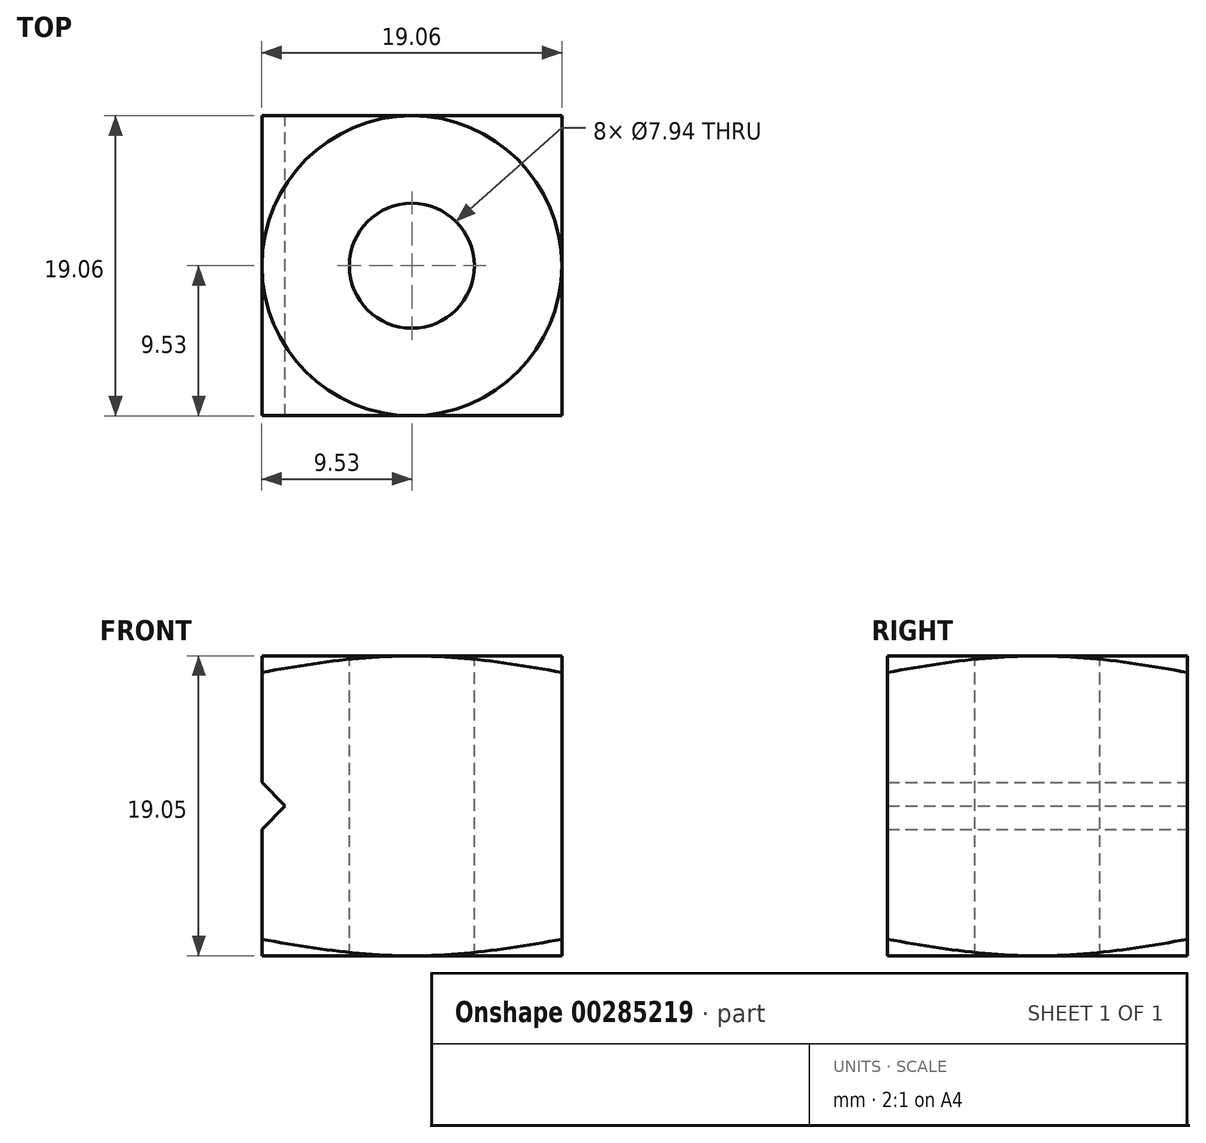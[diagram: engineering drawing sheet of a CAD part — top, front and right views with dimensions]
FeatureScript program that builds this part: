
annotation { "Feature Type Name" : "Feature", "Feature Type Description" : "" }
export const myFeature = defineFeature(function(context is Context, id is Id, definition is map)
    precondition{}
    {
        {
            var Q0;
            Q0=qCreatedBy(makeId("Top.planeOp"),FACE);
            var sketch = newSketch(context, id + "F0", { "sketchPlane" : qUnion([Q0])});
            skLineSegment(sketch, "E0.bottom", {"start": v(9.52, -9.52) * mm, "end": v(-9.53, -9.52) * mm});
            skLineSegment(sketch, "E0.top", {"start": v(9.52, 9.53) * mm, "end": v(-9.53, 9.53) * mm});
            skLineSegment(sketch, "E0.left", {"start": v(9.52, -9.52) * mm, "end": v(9.52, 9.53) * mm});
            skLineSegment(sketch, "E0.right", {"start": v(-9.53, -9.52) * mm, "end": v(-9.53, 9.52) * mm});
            skPoint(sketch, "E0.middle", {"position": v(0, 0) * mm});
            skSolve(sketch);
        }
        {
            var Q0;
            Q0=qSketchRegion(id+"F0",true);
            extrude(context, id + "F1", {"entities" : qUnion([Q0]), "depth" : 19.05 * mm});
        }
        {
            var Q0;
            Q0=makeQuery(id+"F1.opExtrude","CAP_FACE",FACE,{"disambiguationData":[OSD([sQuery(id+"F0.wireOp",EDGE,"E0.bottom"),sQuery(id+"F0.wireOp",EDGE,"E0.top"),sQuery(id+"F0.wireOp",EDGE,"E0.left"),sQuery(id+"F0.wireOp",EDGE,"E0.right")])],"isStart":false});
            var sketch = newSketch(context, id + "F2", { "sketchPlane" : qUnion([Q0])});
            skCircle(sketch, "E1", {"center": v(0, 0) * mm, "radius": 9.53 * mm});
            skCircle(sketch, "E2", {"center": v(0, 0) * mm, "radius": 3.97 * mm});
            skSolve(sketch);
        }
        {
            var Q0;
            Q0=makeQuery(id+"F2.imprint","IMPRINT",FACE,{"disambiguationData":[TD([[makeQuery(id+"F2.imprint","IMPRINT",EDGE,{"derivedFrom":sQuery(id+"F2.wireOp",EDGE,"E2")}),1.0]])]});
            var Q1;
            Q1=sQuery(id+"F2.wireOp",EDGE,"E2");
            extrude(context, id + "F3", {"entities" : qUnion([Q0]), "operationType" : NewBodyOperationType.REMOVE, "surfaceEntities" : qUnion([Q1]), "endBound" : BoundingType.THROUGH_ALL, "oppositeDirection" : true, "depth" : 25.4 * mm});
        }
        {
            var Q0;
            Q0=qCreatedBy(makeId("Right.planeOp"),FACE);
            var sketch = newSketch(context, id + "F4", { "sketchPlane" : qUnion([Q0])});
            skLineSegment(sketch, "E3.0", {"start": v(-9.53, 19.05) * mm, "end": v(9.53, 19.05) * mm});
            skLineSegment(sketch, "E4.0", {"start": v(9.53, 19.05) * mm, "end": v(9.53, 0) * mm});
            skLineSegment(sketch, "E5", {"start": v(9.53, 19.05) * mm, "end": v(24.77, 19.05) * mm});
            skLineSegment(sketch, "E6", {"start": v(24.77, 19.05) * mm, "end": v(24.77, 14.97) * mm});
            skLineSegment(sketch, "E7", {"start": v(9.53, 19.05) * mm, "end": v(24.77, 14.97) * mm});
            skSolve(sketch);
        }
        {
            var Q0;
            Q0=makeQuery(id+"F4.imprint","IMPRINT",FACE,{"disambiguationData":[TD([[makeQuery(id+"F4.imprint","IMPRINT",EDGE,{"derivedFrom":sQuery(id+"F4.wireOp",EDGE,"E5")}),-1.0]])]});
            var Q1;
            Q1=sQuery(id+"F2.wireOp",EDGE,"E1");
            revolve(context, id + "F5", {"operationType" : NewBodyOperationType.REMOVE, "entities" : qUnion([Q0]), "axis" : qUnion([Q1]), "revolveType" : RevolveType.FULL, "oppositeDirection" : true});
        }
        {
            var Q0;
            Q0=makeQuery(id+"F1.opExtrude","CAP_FACE",FACE,{"disambiguationData":[OSD([sQuery(id+"F0.wireOp",EDGE,"E0.bottom"),sQuery(id+"F0.wireOp",EDGE,"E0.top"),sQuery(id+"F0.wireOp",EDGE,"E0.left"),sQuery(id+"F0.wireOp",EDGE,"E0.right")])],"isStart":true});
            var sketch = newSketch(context, id + "F6", { "sketchPlane" : qUnion([Q0])});
            skCircle(sketch, "E8.0", {"center": v(0, 0) * mm, "radius": 9.53 * mm});
            skSolve(sketch);
        }
        {
            var Q0;
            Q0=qCreatedBy(makeId("Right.planeOp"),FACE);
            var sketch = newSketch(context, id + "F7", { "sketchPlane" : qUnion([Q0])});
            skLineSegment(sketch, "E9.0", {"start": v(-9.53, 0) * mm, "end": v(9.53, 0) * mm});
            skLineSegment(sketch, "E10", {"start": v(-9.53, 0) * mm, "end": v(-22.83, 0) * mm});
            skLineSegment(sketch, "E11", {"start": v(-22.83, 0) * mm, "end": v(-22.83, 3.57) * mm});
            skLineSegment(sketch, "E12", {"start": v(-22.83, 3.57) * mm, "end": v(-9.53, 0) * mm});
            skSolve(sketch);
        }
        {
            var Q0;
            Q0=makeQuery(id+"F7.imprint","IMPRINT",FACE,{"disambiguationData":[TD([[makeQuery(id+"F7.imprint","IMPRINT",EDGE,{"derivedFrom":sQuery(id+"F7.wireOp",EDGE,"E10")}),-1.0]])]});
            var Q1;
            Q1=sQuery(id+"F6.wireOp",EDGE,"E8.0");
            revolve(context, id + "F8", {"operationType" : NewBodyOperationType.REMOVE, "entities" : qUnion([Q0]), "axis" : qUnion([Q1]), "revolveType" : RevolveType.FULL, "oppositeDirection" : true});
        }
        {
            var Q0;
            Q0=qCreatedBy(makeId("Front.planeOp"),FACE);
            var sketch = newSketch(context, id + "F9", { "sketchPlane" : qUnion([Q0])});
            skLineSegment(sketch, "E13.0.0", {"start": v(-9.53, 18) * mm, "end": v(-9.53, 1.06) * mm});
            skFitSpline(sketch, "E13.0.1", {"points": [v(-9.53, 1.06) * mm, v(-7.95, 0.76) * mm, v(-5.57, 0.36) * mm, v(-2.39, 0.05) * mm, v(-0.8, 0) * mm, v(0, 0) * mm]});
            skFitSpline(sketch, "E13.0.2", {"points": [v(0, 0) * mm, v(0.8, 0) * mm, v(2.39, 0.05) * mm, v(4.78, 0.28) * mm, v(7.16, 0.63) * mm, v(8.74, 0.9) * mm, v(9.52, 1.06) * mm]});
            skLineSegment(sketch, "E13.0.3", {"start": v(9.52, 1.06) * mm, "end": v(9.52, 18) * mm});
            skFitSpline(sketch, "E13.0.4", {"points": [v(9.52, 11.64) * mm, v(8.74, 11.8) * mm, v(7.16, 12.07) * mm, v(4.78, 12.42) * mm, v(2.39, 12.65) * mm, v(0.8, 12.7) * mm, v(0, 12.7) * mm]});
            skFitSpline(sketch, "E13.0.5", {"points": [v(0, 12.7) * mm, v(-0.8, 12.7) * mm, v(-2.39, 12.65) * mm, v(-5.57, 12.34) * mm, v(-7.95, 11.94) * mm, v(-9.53, 11.64) * mm]});
            skFitSpline(sketch, "E14.0.0", {"points": [v(0, 12.7) * mm, v(-0.8, 12.7) * mm, v(-2.39, 12.65) * mm, v(-5.57, 12.34) * mm, v(-7.95, 11.94) * mm, v(-9.53, 11.64) * mm]});
            skLineSegment(sketch, "E14.0.1", {"start": v(0, 19.05) * mm, "end": v(-9.53, 19.05) * mm});
            skFitSpline(sketch, "E14.0.2", {"points": [v(-9.53, 12.7) * mm, v(-9.53, 12.35) * mm, v(-9.53, 12) * mm, v(-9.53, 11.64) * mm]});
            skLineSegment(sketch, "E15.0.0", {"start": v(-9.53, 0) * mm, "end": v(0, 0) * mm});
            skFitSpline(sketch, "E15.0.1", {"points": [v(0, 0) * mm, v(-0.8, 0) * mm, v(-2.39, 0.05) * mm, v(-5.57, 0.36) * mm, v(-7.95, 0.76) * mm, v(-9.53, 1.06) * mm]});
            skFitSpline(sketch, "E15.0.2", {"points": [v(-9.53, 0) * mm, v(-9.53, 0.35) * mm, v(-9.53, 0.7) * mm, v(-9.53, 1.06) * mm]});
            skFitSpline(sketch, "E16.0.1", {"points": [v(-9.53, 1.06) * mm, v(-7.95, 0.76) * mm, v(-5.57, 0.36) * mm, v(-2.39, 0.05) * mm, v(-0.8, 0) * mm, v(0, 0) * mm]});
            skFitSpline(sketch, "E16.0.2", {"points": [v(0, 0) * mm, v(0.8, 0) * mm, v(2.39, 0.05) * mm, v(4.78, 0.28) * mm, v(7.16, 0.63) * mm, v(8.74, 0.9) * mm, v(9.52, 1.06) * mm]});
            skFitSpline(sketch, "E16.0.4", {"points": [v(9.52, 11.64) * mm, v(8.74, 11.8) * mm, v(7.16, 12.07) * mm, v(4.78, 12.42) * mm, v(2.39, 12.65) * mm, v(0.8, 12.7) * mm, v(0, 12.7) * mm]});
            skFitSpline(sketch, "E16.0.5", {"points": [v(0, 12.7) * mm, v(-0.8, 12.7) * mm, v(-2.39, 12.65) * mm, v(-5.57, 12.34) * mm, v(-7.95, 11.94) * mm, v(-9.53, 11.64) * mm]});
            skLineSegment(sketch, "E17", {"start": v(-9.53, 9.52) * mm, "end": v(-9.53, 8.8) * mm});
            skLineSegment(sketch, "E18", {"start": v(-10.38, 7.94) * mm, "end": v(-9.53, 8.8) * mm});
            skLineSegment(sketch, "E19", {"start": v(-10.38, 7.94) * mm, "end": v(-9.53, 9.52) * mm});
            skLineSegment(sketch, "E20", {"start": v(-9.53, 7.08) * mm, "end": v(-10.38, 7.94) * mm});
            skLineSegment(sketch, "E21", {"start": v(-9.53, 7.08) * mm, "end": v(-9.53, 8.8) * mm});
            skSolve(sketch);
        }
        {
            var Q0;
            {var subQ0=sQuery(id+"F9.wireOp",EDGE,"E18");Q0=makeQuery(id+"F9.imprint","IMPRINT",FACE,{"disambiguationData":[TD([[makeQuery(id+"F9.imprint","IMPRINT",EDGE,{"derivedFrom":subQ0}),1.0]])]});}
            extrude(context, id + "F10", {"entities" : qUnion([Q0]), "operationType" : NewBodyOperationType.REMOVE, "endBound" : BoundingType.SYMMETRIC, "oppositeDirection" : true, "depth" : 25.4 * mm});
        }
        {
            var Q0;
            Q0=makeQuery(id+"F1.opExtrude","SWEPT_FACE",FACE,{"disambiguationData":[OSD([sQuery(id+"F0.wireOp",EDGE,"E0.top")])]});
            var sketch = newSketch(context, id + "F11", { "sketchPlane" : qUnion([Q0])});
            skLineSegment(sketch, "E22", {"start": v(9.53, 9.53) * mm, "end": v(8.04, 9.53) * mm});
            skLineSegment(sketch, "E23", {"start": v(8.04, 9.53) * mm, "end": v(9.53, 8.04) * mm});
            skLineSegment(sketch, "E24", {"start": v(8.04, 9.53) * mm, "end": v(9.53, 11.01) * mm});
            skSolve(sketch);
        }
        {
            var Q0;
            {var subQ0=sQuery(id+"F11.wireOp",EDGE,"E22");Q0=makeQuery(id+"F11.imprint","IMPRINT",FACE,{"disambiguationData":[TD([[makeQuery(id+"F11.imprint","IMPRINT",EDGE,{"derivedFrom":subQ0}),1.0]])]});}
            var Q1;
            {var subQ0=sQuery(id+"F11.wireOp",EDGE,"E22");Q1=makeQuery(id+"F11.imprint","IMPRINT",FACE,{"disambiguationData":[TD([[makeQuery(id+"F11.imprint","IMPRINT",EDGE,{"derivedFrom":subQ0}),-1.0]])]});}
            extrude(context, id + "F12", {"entities" : qUnion([Q0, Q1]), "operationType" : NewBodyOperationType.REMOVE, "oppositeDirection" : true, "depth" : 25.4 * mm});
        }
    });
